# Revit family: QF_Summit_DW244SSADA_Built_In Dishwasher_ADA Compliant
name_source: partatom
category: Specialty Equipment
units: mm (PartAtom-declared; Revit-internal decimal feet)

## family parameters
Always vertical = Yes
Cut with Voids When Loaded = No
Part Type = Normal
Room Calculation Point = No
Round Connector Dimension = Use Diameter
Shared = No
Work Plane-Based = No

## types (1)
- QF_Summit_DW244SSADA_Built_In Dishwasher_ADA Compliant
    Apparent Power = 1380 VA
    Cold Water Connection Height = 0"
    Cold Water Flow = 0 GPM
    Cold Water Maximum Pressure = 0.00 psi
    Cold Water Minimum Pressure = 0.00 psi
    Cold Water RI Height = 0"
    Cold Water Size = 1"
    Cold Water Temperature Recommended = -460 °F
    Conn Conduit = Yes
    Cycle = 60 Hz
    Default Elevation = 0"
    Depth = 24 1/4"
    Description = Built-In Dishwasher ADA Compliant
    Elec Conn Connection Height = 0"
    Elec Conn RI Height = 0"
    FL Amps = 12 A
    Foodservice Equipment Identifier = Yes
    Identify Quantity as Lot = Yes
    Indirect Waste Connection Height = 0"
    Indirect Waste Flow = 0 GPM
    Indirect Waste Size = 1"
    Length = 23 1/2"
    Manufacturer = Summit
    Max Overcurrent Protection = 0 A
    Min Ckt Ampacity = 0 A
    Model = DW244SSADA
    Number of Poles = 1
    Phase = 1
    Volts = 115 V
    Waste Water Discharge Temperature = -460 °F
    Watts = 1380 W
    Weight in Pounds = 95

## geometry (parser evidence)
native form markers: Sweep x4
no freeform markers — native parametric forms only
